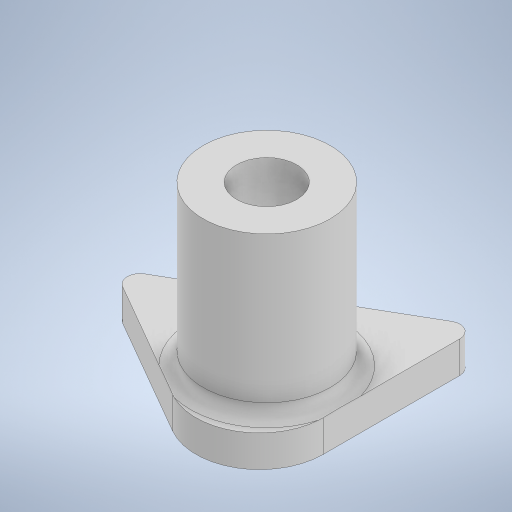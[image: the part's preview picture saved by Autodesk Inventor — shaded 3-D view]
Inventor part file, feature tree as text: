
AUTODESK INVENTOR PART (.ipt)
format: ipt  version: 2023 (Build 270158000, 158)  size: 272,896 bytes
history: native  units: in
note: dims shown in document units (in); Inventor stores cm internally (conversion verified against a paired STEP export)
features: other x4, extrude x1, sketch x1, projected_geometry x1
ambient origin geometry x8: Origin, YZ Plane, XZ Plane, XY Plane, X Axis, Y Axis, Z Axis, Center Point
bodies: Body1 (feature_tree)
feature tree (7):
  other  "base.ipt"
  extrude  "Extrusion1"  Depth=0.3937in TaperAngle=0.0deg
  other  "Tight_Bushing::base.ipt"
  other  "TaggingFeature1"
  sketch  "Sketch1"  dims[d0=0.3937in d1=0.3937in d2=0.0in]
  projected_geometry  "Projected Loop1"
  other  "Tight_Bushing"
